# Revit family: Gewindestange VA
name_source: partatom
category: HLS-Bauteile
revit_build: Autodesk Revit 2017 (Build: 20190507_1515(x64)
units: mm (PartAtom-declared; Revit-internal decimal feet)

## family parameters
Arbeitsebenenbasiert = Nein
Beim Laden mit Abzugskörper schneiden = Nein
Bemaßung runder Anschluss = Durchmesser verwenden
Gemeinsam genutzt = Ja
Immer vertikal = Nein
Raumberechnungspunkt = Nein
Teiletyp = Normal

## types (8) — shared parameters
Fabrikat = MEFA
Firma = MEFA Befestigungs- und Montagesysteme GmbH
Material = Edelstahl
Mengeneinheit = St
Montagelänge = 1000 mm  [stored 3.28084 ft]

## per-type parameters (varying)
| type | Artikelnummer | D | EAN | Gewicht | Gewicht pro Bauteil | Gewicht pro Stück | Kurztext1 | Kurztext2 | vpe |
| Gewindestange M 8x1000 V2A | 0738006 | 7 mm  [stored 0.0229659 ft] | 4250928417015 | 0.33 kg | 0.33 kg | 0.33 kg | Gewindestange DIN 976-1 V2A | M8 x 1000 mm | 50 St |
| Gewindestange M10x1000 V2A | 0738009 | 8 mm  [stored 0.0262467 ft] | 4250928417022 | 0.52 kg | 0.52 kg | 0.52 kg | Gewindestange DIN 976-1 V2A | M10 x 1000 mm | 25 St |
| Gewindestange M12x1000 V2A | 0738012 | 10 mm  [stored 0.0328084 ft] | 4250928417039 | 0.75 kg | 0.75 kg | 0.75 kg | Gewindestange DIN 976-1 V2A | M12 x 1000 mm | 25 St |
| Gewindestange M16x1000 V2A | 0738016 | 14 mm  [stored 0.0459318 ft] | 4250928417046 | 1.33 kg | 1.33 kg | 1.33 kg | Gewindestange DIN 976-1 V2A | M16 x 1000 mm | 10 St |
| Gewindestange M 8x1000 V4A | 0738508 | 7 mm  [stored 0.0229659 ft] | 4250928417053 | 0.33 kg | 0.33 kg | 0.33 kg | Gewindestange DIN 976-1 V4A | M8 x 1000 mm | 50 St |
| Gewindestange M10x1000 V4A | 0738510 | 8 mm  [stored 0.0262467 ft] | 4250928417060 | 0.52 kg | 0.52 kg | 0.52 kg | Gewindestange DIN 976-1 V4A | M10 x 1000 mm | 25 St |
| Gewindestange M12x1000 V4A | 0738512 | 10 mm  [stored 0.0328084 ft] | 4250928417077 | 0.75 kg | 0.75 kg | 0.75 kg | Gewindestange DIN 976-1 V4A | M12 x 1000 mm | 25 St |
| Gewindestange M16x1000 V4A | 0738516 | 14 mm  [stored 0.0459318 ft] | 4250928417084 | 1.33 kg | 1.33 kg | 1.33 kg | Gewindestange DIN 976-1 V4A | M16 x 1000 mm | 10 St |

note: [stored X ft] marks values corroborated as IEEE doubles in the binary element streams (Revit-internal decimal feet)
